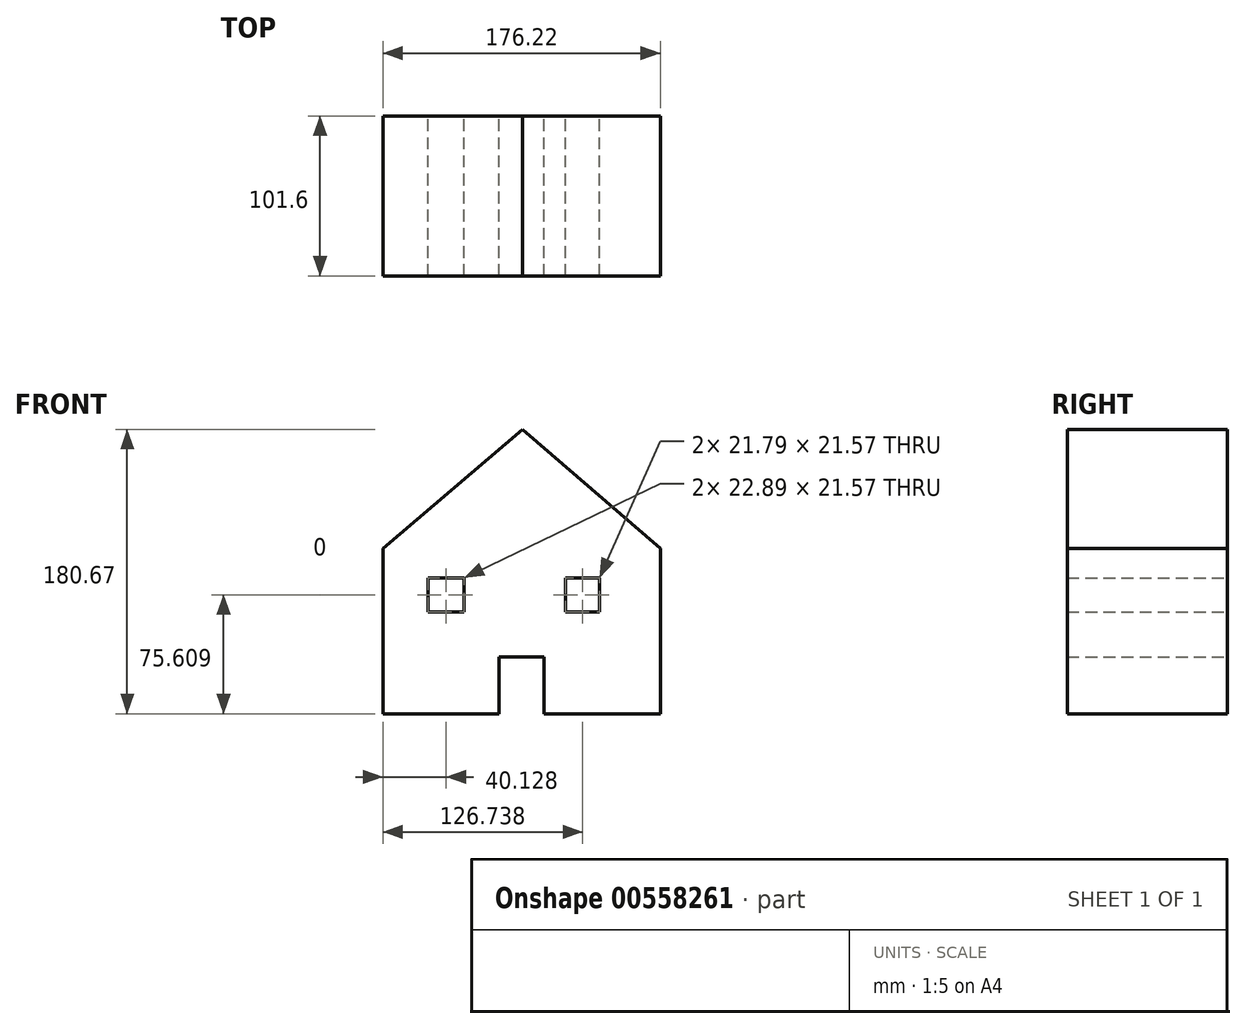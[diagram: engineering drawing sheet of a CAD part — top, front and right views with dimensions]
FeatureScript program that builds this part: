
annotation { "Feature Type Name" : "Feature", "Feature Type Description" : "" }
export const myFeature = defineFeature(function(context is Context, id is Id, definition is map)
    precondition{}
    {
        {
            var Q0;
            Q0=qCreatedBy(makeId("Front.planeOp"),FACE);
            var sketch = newSketch(context, id + "F0", { "sketchPlane" : qUnion([Q0])});
            skLineSegment(sketch, "E0", {"start": v(-88.68, 30.22) * mm, "end": v(-88.68, -74.92) * mm});
            skLineSegment(sketch, "E1", {"start": v(87.54, -74.92) * mm, "end": v(87.54, 30.22) * mm});
            skLineSegment(sketch, "E2", {"start": v(-88.68, 30.22) * mm, "end": v(0, 105.75) * mm});
            skLineSegment(sketch, "E3", {"start": v(0, 105.75) * mm, "end": v(87.54, 30.22) * mm});
            skLineSegment(sketch, "E4", {"start": v(0, 105.75) * mm, "end": v(0, 105.75) * mm});
            skLineSegment(sketch, "E5", {"start": v(-15.1, -74.92) * mm, "end": v(-15.1, -38.7) * mm});
            skLineSegment(sketch, "E6", {"start": v(-88.68, -74.92) * mm, "end": v(-15.1, -74.92) * mm});
            skLineSegment(sketch, "E7", {"start": v(87.54, -74.92) * mm, "end": v(13.52, -74.92) * mm});
            skLineSegment(sketch, "E8", {"start": v(13.52, -74.92) * mm, "end": v(13.52, -38.7) * mm});
            skLineSegment(sketch, "E9", {"start": v(-15.1, -38.7) * mm, "end": v(13.52, -38.7) * mm});
            skLineSegment(sketch, "E10", {"start": v(-60, -10.1) * mm, "end": v(-37.1, -10.1) * mm});
            skLineSegment(sketch, "E11", {"start": v(-37.1, -10.1) * mm, "end": v(-37.1, 11.47) * mm});
            skLineSegment(sketch, "E12", {"start": v(-37.1, 11.47) * mm, "end": v(-60, 11.47) * mm});
            skLineSegment(sketch, "E13", {"start": v(-60, 11.47) * mm, "end": v(-60, -10.1) * mm});
            skLineSegment(sketch, "E14", {"start": v(27.16, 11.47) * mm, "end": v(27.16, -10.1) * mm});
            skLineSegment(sketch, "E15", {"start": v(27.16, -10.1) * mm, "end": v(48.95, -10.1) * mm});
            skLineSegment(sketch, "E16", {"start": v(48.95, -10.32) * mm, "end": v(48.95, 11.47) * mm});
            skLineSegment(sketch, "E17", {"start": v(48.95, 11.47) * mm, "end": v(24.52, 11.47) * mm});
            skSolve(sketch);
        }
        {
            var Q0;
            Q0 = qSketchRegion(id + "F0", true);
            extrude(context, id + "F1", {"entities" : qUnion([Q0]), "depth" : 101.6 * mm, "offsetDistance" : 25.4 * mm});
        }
    });
